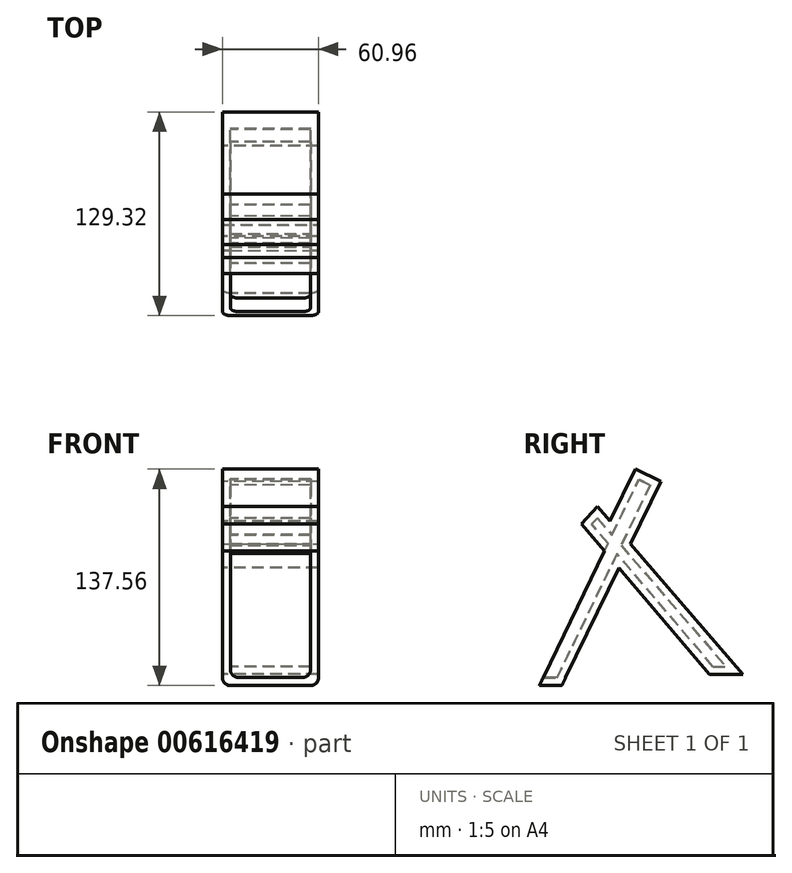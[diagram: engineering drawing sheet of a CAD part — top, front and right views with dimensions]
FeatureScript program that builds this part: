
annotation { "Feature Type Name" : "Feature", "Feature Type Description" : "" }
export const myFeature = defineFeature(function(context is Context, id is Id, definition is map)
    precondition{}
    {
        {
            var Q0;
            Q0=qCreatedBy(makeId("Right.planeOp"),FACE);
            var sketch = newSketch(context, id + "F0", { "sketchPlane" : qUnion([Q0])});
            skLineSegment(sketch, "E0", {"start": v(-60.83, -63.46) * mm, "end": v(0, 62.17) * mm});
            skLineSegment(sketch, "E1", {"start": v(0, 62.17) * mm, "end": v(0, 62.17) * mm});
            skLineSegment(sketch, "E2", {"start": v(0, 62.17) * mm, "end": v(7, 58.78) * mm});
            skLineSegment(sketch, "E3", {"start": v(7, 58.78) * mm, "end": v(7, 58.78) * mm});
            skLineSegment(sketch, "E4", {"start": v(7, 58.78) * mm, "end": v(-52.22, -63.5) * mm});
            skLineSegment(sketch, "E5", {"start": v(-52.22, -63.5) * mm, "end": v(-52.22, -63.5) * mm});
            skLineSegment(sketch, "E6", {"start": v(-52.22, -63.5) * mm, "end": v(-60.83, -63.46) * mm});
            skSolve(sketch);
        }
        {
            var Q0;
            Q0 = qSketchRegion(id + "F0", true);
            extrude(context, id + "F1", {"entities" : qUnion([Q0]), "depth" : 25.4 * mm, "offsetDistance" : 25.4 * mm, "hasSecondDirection" : true, "secondDirectionOppositeDirection" : true, "secondDirectionDepth" : 25.4 * mm});
        }
        {
            var Q0;
            Q0=qCreatedBy(makeId("Right.planeOp"),FACE);
            var sketch = newSketch(context, id + "F2", { "sketchPlane" : qUnion([Q0])});
            skLineSegment(sketch, "E7", {"start": v(-26.44, 37.67) * mm, "end": v(54.92, -56.32) * mm});
            skLineSegment(sketch, "E8", {"start": v(54.92, -56.32) * mm, "end": v(54.92, -56.32) * mm});
            skLineSegment(sketch, "E9", {"start": v(47.07, -56.32) * mm, "end": v(54.92, -56.32) * mm});
            skLineSegment(sketch, "E10", {"start": v(47.07, -56.32) * mm, "end": v(-29.83, 33.96) * mm});
            skLineSegment(sketch, "E11", {"start": v(-29.83, 33.96) * mm, "end": v(-26.44, 37.67) * mm});
            skSolve(sketch);
        }
        {
            var Q0;
            Q0 = qSketchRegion(id + "F2", true);
            extrude(context, id + "F3", {"entities" : qUnion([Q0]), "operationType" : NewBodyOperationType.ADD, "depth" : 25.4 * mm, "offsetDistance" : 25.4 * mm, "hasSecondDirection" : true, "secondDirectionOppositeDirection" : true, "secondDirectionDepth" : 25.4 * mm});
        }
        {
            var Q0;
            {var subQ4=sQuery(id+"F0.wireOp",EDGE,"E6");var subQ7=sQuery(id+"F0.wireOp",EDGE,"E0");Q0=makeQuery(id+"F3.boolean.opBoolean","SPLIT",FACE,{"disambiguationData":[TD([makeQuery(id+"F1.opExtrude","SWEPT_FACE",FACE,{"disambiguationData":[OSD([subQ4])]})])],"derivedFrom":makeQuery(id+"F1.opExtrude","SWEPT_FACE",FACE,{"disambiguationData":[OSD([subQ7])]})});}
            shell(context, id + "F4", {"entities" : qUnion([Q0]), "thickness" : 5.08 * mm, "oppositeDirection" : true});
        }
        {
            var Q0;
            Q0=makeQuery(id+"F1.opExtrude","CAP_EDGE",EDGE,{"disambiguationData":[OSD([sQuery(id+"F0.wireOp",EDGE,"E6")])],"isStart":true});
            var Q1;
            Q1=makeQuery(id+"F1.opExtrude","CAP_EDGE",EDGE,{"disambiguationData":[OSD([sQuery(id+"F0.wireOp",EDGE,"E6")])],"isStart":false});
            fillet(context, id + "F5", {"entities" : qUnion([Q0, Q1]), "radius" : 5.08 * mm, "tangentPropagation" : true, "allowEdgeOverflow" : false});
        }
        {
            var Q0;
            {var subQ0=sQuery(id+"F0.wireOp",EDGE,"E6");Q0=makeQuery(id+"F4.opShell","OFFSET_EDGE",EDGE,{"disambiguationData":[OSD([subQ0]),TDD([makeQuery(id+"F1.opExtrude","CAP_EDGE",EDGE,{"disambiguationData":[OSD([subQ0])],"isStart":true})])]});}
            var Q1;
            {var subQ0=sQuery(id+"F0.wireOp",EDGE,"E6");Q1=makeQuery(id+"F4.opShell","OFFSET_EDGE",EDGE,{"disambiguationData":[OSD([subQ0]),TDD([makeQuery(id+"F1.opExtrude","CAP_EDGE",EDGE,{"disambiguationData":[OSD([subQ0])],"isStart":false})])]});}
            fillet(context, id + "F6", {"entities" : qUnion([Q0, Q1]), "radius" : 5.08 * mm, "tangentPropagation" : true, "allowEdgeOverflow" : false});
        }
        {
            var Q0;
            {var subQ1=sQuery(id+"F2.wireOp",EDGE,"E10");var subQ5=sQuery(id+"F0.wireOp",EDGE,"E4");Q0=makeQuery(id+"F3.boolean.opBoolean","SPLIT",FACE,{"disambiguationData":[TD([makeQuery(id+"F1.opExtrude","SWEPT_FACE",FACE,{"disambiguationData":[OSD([subQ5])]})])],"derivedFrom":makeQuery(id+"F3.opExtrude","SWEPT_FACE",FACE,{"disambiguationData":[OSD([subQ1])]})});}
            shell(context, id + "F7", {"entities" : qUnion([Q0]), "thickness" : 0.25 * mm});
        }
    });
